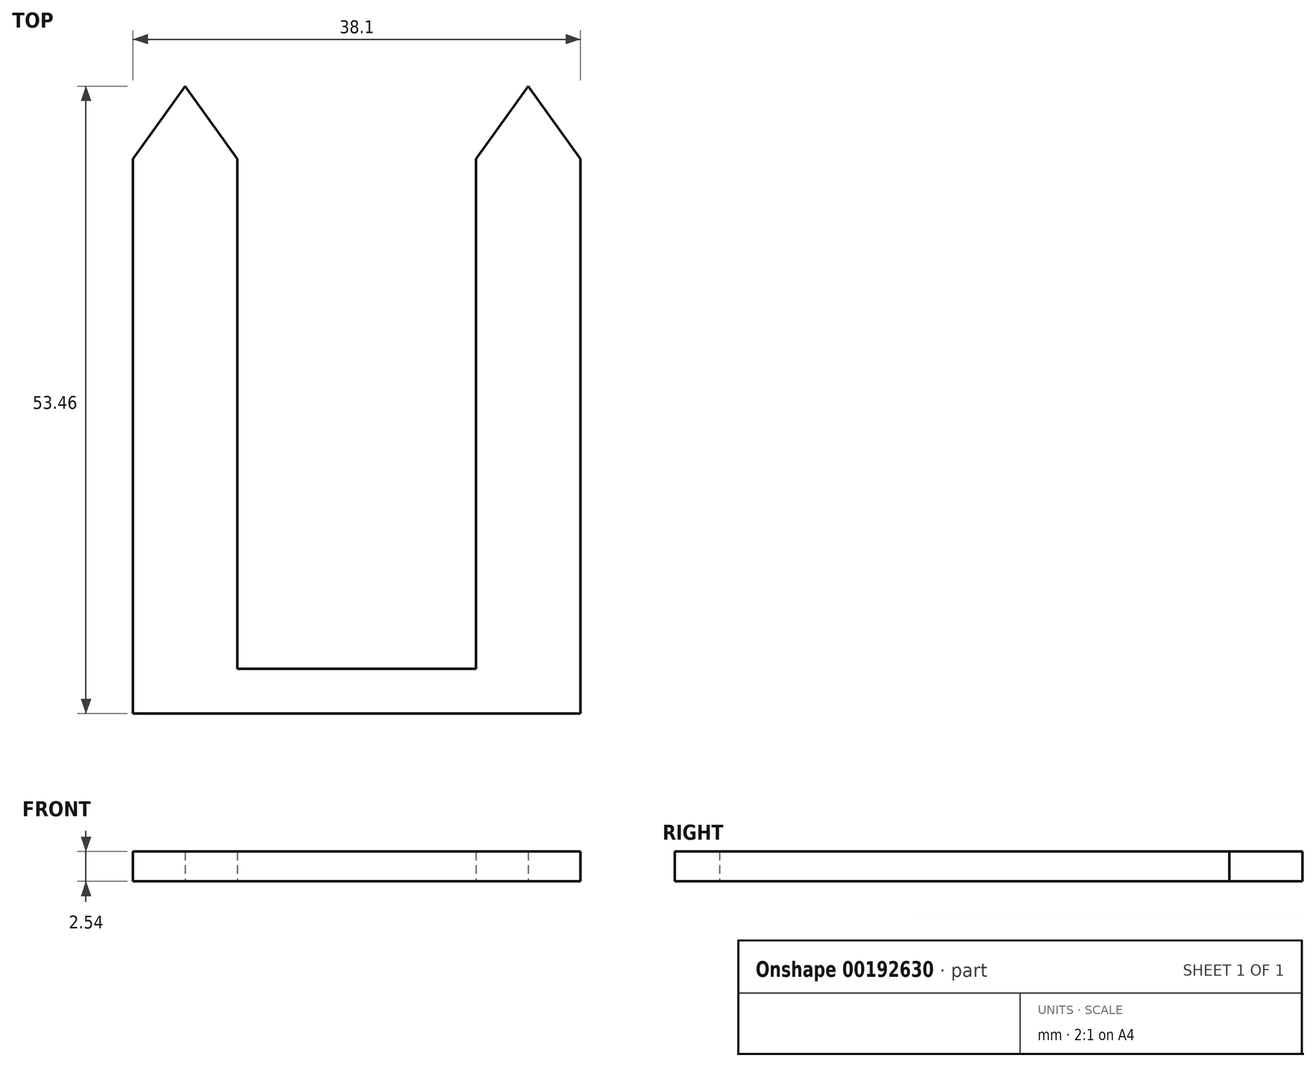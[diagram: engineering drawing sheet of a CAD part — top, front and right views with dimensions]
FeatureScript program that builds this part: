
annotation { "Feature Type Name" : "Feature", "Feature Type Description" : "" }
export const myFeature = defineFeature(function(context is Context, id is Id, definition is map)
    precondition{}
    {
        {
            var Q0;
            Q0=qCreatedBy(makeId("Top.planeOp"),FACE);
            var sketch = newSketch(context, id + "F0", { "sketchPlane" : qUnion([Q0])});
            skLineSegment(sketch, "E0.bottom", {"start": v(19.05, 1.9) * mm, "end": v(-19.05, 1.9) * mm});
            skLineSegment(sketch, "E0.top", {"start": v(19.05, -1.9) * mm, "end": v(-19.05, -1.9) * mm});
            skLineSegment(sketch, "E0.left", {"start": v(19.05, 1.9) * mm, "end": v(19.05, -1.9) * mm});
            skLineSegment(sketch, "E0.right", {"start": v(-19.05, 1.9) * mm, "end": v(-19.05, -1.9) * mm});
            skPoint(sketch, "E0.middle", {"position": v(0, 0) * mm});
            skLineSegment(sketch, "E1.bottom", {"start": v(-19.05, 1.9) * mm, "end": v(-10.16, 1.9) * mm});
            skLineSegment(sketch, "E1.top", {"start": v(-19.05, 45.33) * mm, "end": v(-10.16, 45.33) * mm});
            skLineSegment(sketch, "E1.left", {"start": v(-19.05, 1.9) * mm, "end": v(-19.05, 45.33) * mm});
            skLineSegment(sketch, "E1.right", {"start": v(-10.16, 1.9) * mm, "end": v(-10.16, 45.33) * mm});
            skLineSegment(sketch, "E2.bottom", {"start": v(19.05, 1.9) * mm, "end": v(10.16, 1.9) * mm});
            skLineSegment(sketch, "E2.top", {"start": v(19.05, 45.33) * mm, "end": v(10.16, 45.33) * mm});
            skLineSegment(sketch, "E2.left", {"start": v(19.05, 1.9) * mm, "end": v(19.05, 45.33) * mm});
            skLineSegment(sketch, "E2.right", {"start": v(10.16, 1.9) * mm, "end": v(10.16, 45.33) * mm});
            skLineSegment(sketch, "E3", {"start": v(-14.6, 45.33) * mm, "end": v(-14.6, 51.55) * mm});
            skLineSegment(sketch, "E4", {"start": v(-19.05, 45.33) * mm, "end": v(-14.6, 51.55) * mm});
            skLineSegment(sketch, "E5", {"start": v(-14.6, 51.55) * mm, "end": v(-10.16, 45.33) * mm});
            skLineSegment(sketch, "E6", {"start": v(14.6, 45.33) * mm, "end": v(14.6, 51.55) * mm});
            skLineSegment(sketch, "E7", {"start": v(10.16, 45.33) * mm, "end": v(14.6, 51.55) * mm});
            skLineSegment(sketch, "E8", {"start": v(14.6, 51.55) * mm, "end": v(19.05, 45.33) * mm});
            skSolve(sketch);
        }
        {
            var Q0;
            Q0 = qSketchRegion(id + "F0", true);
            extrude(context, id + "F1", {"entities" : qUnion([Q0]), "depth" : 2.54 * mm});
        }
    });
